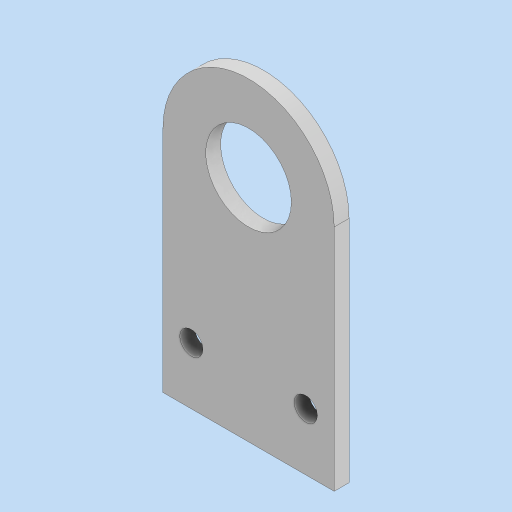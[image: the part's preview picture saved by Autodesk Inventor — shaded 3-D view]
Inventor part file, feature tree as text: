
AUTODESK INVENTOR PART (.ipt)
format: ipt  version: 2024 (Build 280153000, 153)  size: 110,592 bytes
history: native  units: in
note: dims shown in document units (in); Inventor stores cm internally (conversion verified against a paired STEP export)
features: extrude x1, sketch x1
ambient origin geometry x8: Origin, YZ Plane, XZ Plane, XY Plane, X Axis, Y Axis, Z Axis, Center Point
bodies: Solid1 (feature_tree)
feature tree (2):
  extrude  "Extrusion1"  Depth=0.748in
  sketch  "Sketch1"  dims[d0=1.4961in d1=0.748in d8=0.13in d9=0.0in d10=0.203in d11=0.203in d12=0.5in d13=0.5in d14=0.5in d15=0.5in d16=2.0in]
